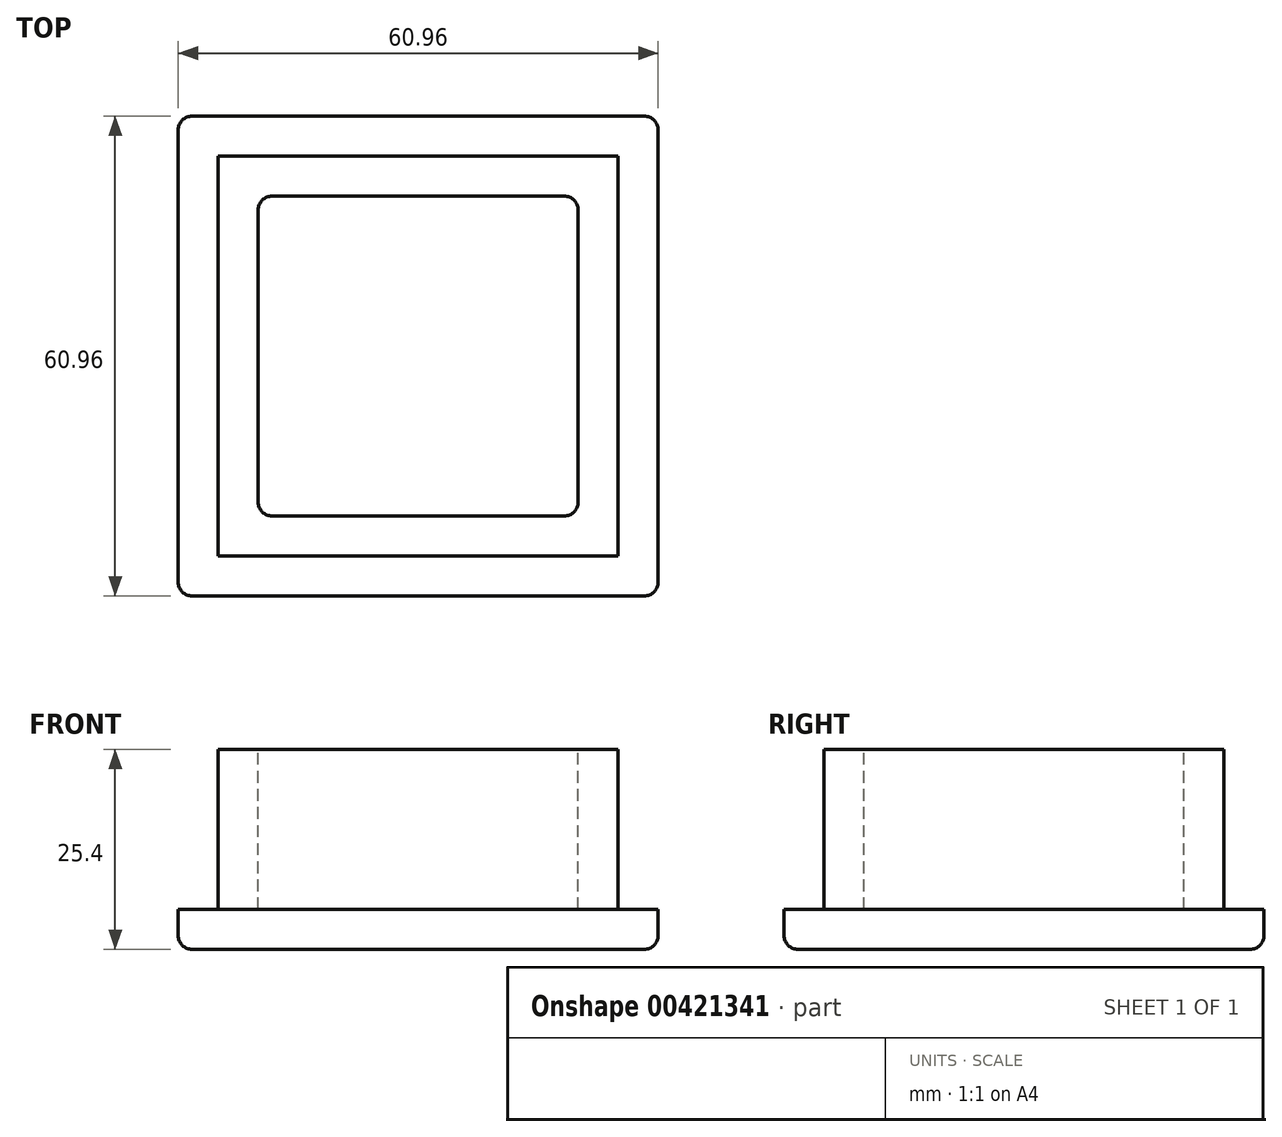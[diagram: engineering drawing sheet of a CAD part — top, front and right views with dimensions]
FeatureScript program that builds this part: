
annotation { "Feature Type Name" : "Feature", "Feature Type Description" : "" }
export const myFeature = defineFeature(function(context is Context, id is Id, definition is map)
    precondition{}
    {
        {
            var Q0;
            Q0=qCreatedBy(makeId("Top.planeOp"),FACE);
            var sketch = newSketch(context, id + "F0", { "sketchPlane" : qUnion([Q0])});
            skLineSegment(sketch, "E0.bottom", {"start": v(0, 0) * mm, "end": v(50.8, 0) * mm});
            skLineSegment(sketch, "E0.top", {"start": v(0, 50.8) * mm, "end": v(50.8, 50.8) * mm});
            skLineSegment(sketch, "E0.left", {"start": v(0, 0) * mm, "end": v(0, 50.8) * mm});
            skLineSegment(sketch, "E0.right", {"start": v(50.8, 0) * mm, "end": v(50.8, 50.8) * mm});
            skSolve(sketch);
        }
        {
            var Q0;
            Q0 = qSketchRegion(id + "F0", true);
            extrude(context, id + "F1", {"entities" : qUnion([Q0]), "depth" : 25.4 * mm});
        }
        {
            var Q0;
            Q0=makeQuery(id+"F1.opExtrude","CAP_FACE",FACE,{"disambiguationData":[OSD([sQuery(id+"F0.wireOp",EDGE,"E0.bottom"),sQuery(id+"F0.wireOp",EDGE,"E0.top"),sQuery(id+"F0.wireOp",EDGE,"E0.left"),sQuery(id+"F0.wireOp",EDGE,"E0.right")])],"isStart":false});
            var sketch = newSketch(context, id + "F2", { "sketchPlane" : qUnion([Q0])});
            skLineSegment(sketch, "E1.bottom", {"start": v(5.08, 5.08) * mm, "end": v(45.72, 5.08) * mm});
            skLineSegment(sketch, "E1.top", {"start": v(5.08, 45.72) * mm, "end": v(45.72, 45.72) * mm});
            skLineSegment(sketch, "E1.left", {"start": v(5.08, 5.08) * mm, "end": v(5.08, 45.72) * mm});
            skLineSegment(sketch, "E1.right", {"start": v(45.72, 5.08) * mm, "end": v(45.72, 45.72) * mm});
            skSolve(sketch);
        }
        {
            var Q0;
            Q0=makeQuery(id+"F2.imprint","IMPRINT",FACE,{"disambiguationData":[TD([[makeQuery(id+"F2.imprint","IMPRINT",EDGE,{"derivedFrom":sQuery(id+"F2.wireOp",EDGE,"E1.bottom")}),1.0]])]});
            extrude(context, id + "F3", {"entities" : qUnion([Q0]), "operationType" : NewBodyOperationType.REMOVE, "oppositeDirection" : true, "depth" : 20.32 * mm});
        }
        {
            var Q0;
            Q0=makeQuery(id+"F3.boolean.opBoolean","COPY",FACE,{"derivedFrom":makeQuery(id+"F3.opExtrude","CAP_FACE",FACE,{"disambiguationData":[OSD([sQuery(id+"F2.wireOp",EDGE,"E1.bottom"),sQuery(id+"F2.wireOp",EDGE,"E1.top"),sQuery(id+"F2.wireOp",EDGE,"E1.left"),sQuery(id+"F2.wireOp",EDGE,"E1.right")])],"isStart":false})});
            var sketch = newSketch(context, id + "F4", { "sketchPlane" : qUnion([Q0])});
            skCircle(sketch, "E2", {"center": v(25.4, 25.4) * mm, "radius": 7.62 * mm});
            skPoint(sketch, "E2.centerSnap0", {"position": v(25.4, 45.72) * mm});
            skSolve(sketch);
        }
        {
            var Q0;
            Q0=makeQuery(id+"F1.opExtrude","CAP_FACE",FACE,{"disambiguationData":[OSD([sQuery(id+"F0.wireOp",EDGE,"E0.bottom"),sQuery(id+"F0.wireOp",EDGE,"E0.top"),sQuery(id+"F0.wireOp",EDGE,"E0.left"),sQuery(id+"F0.wireOp",EDGE,"E0.right")])],"isStart":true});
            var sketch = newSketch(context, id + "F5", { "sketchPlane" : qUnion([Q0])});
            skLineSegment(sketch, "E3.bottom", {"start": v(0, 0) * mm, "end": v(55.88, 0) * mm});
            skLineSegment(sketch, "E3.top", {"start": v(0, -55.88) * mm, "end": v(55.88, -55.88) * mm});
            skLineSegment(sketch, "E3.left", {"start": v(0, 0) * mm, "end": v(0, -55.88) * mm});
            skLineSegment(sketch, "E3.right", {"start": v(55.88, 0) * mm, "end": v(55.88, -55.88) * mm});
            skSolve(sketch);
        }
        {
            var Q0;
            {var subQ4=makeQuery(id+"F1.opExtrude","CAP_EDGE",EDGE,{"disambiguationData":[OSD([sQuery(id+"F0.wireOp",EDGE,"E0.top")])],"isStart":true});Q0=makeQuery(id+"F5.imprint","IMPRINT",FACE,{"disambiguationData":[TD([[makeQuery(id+"F5.imprint","IMPRINT",EDGE,{"derivedFrom":subQ4}),1.0]])]});}
            extrude(context, id + "F6", {"entities" : qUnion([Q0]), "operationType" : NewBodyOperationType.ADD, "depth" : 25.4 * mm});
        }
        {
            var Q0;
            Q0=makeQuery(id+"F6.boolean.opBoolean","MERGE",FACE,{"derivedFrom":[makeQuery(id+"F1.opExtrude","SWEPT_FACE",FACE,{"disambiguationData":[OSD([sQuery(id+"F0.wireOp",EDGE,"E0.left")])]}),makeQuery(id+"F6.opExtrude","SWEPT_FACE",FACE,{"disambiguationData":[OSD([sQuery(id+"F5.wireOp",EDGE,"E3.left")])]})]});
            var sketch = newSketch(context, id + "F7", { "sketchPlane" : qUnion([Q0])});
            skLineSegment(sketch, "E4.bottom", {"start": v(-50.8, -25.4) * mm, "end": v(0, -25.4) * mm});
            skLineSegment(sketch, "E4.top", {"start": v(-50.8, -20.32) * mm, "end": v(0, -20.32) * mm});
            skLineSegment(sketch, "E4.left", {"start": v(-50.8, -25.4) * mm, "end": v(-50.8, -20.32) * mm});
            skLineSegment(sketch, "E4.right", {"start": v(0, -25.4) * mm, "end": v(0, -20.32) * mm});
            skSolve(sketch);
        }
        {
            var Q0;
            Q0=makeQuery(id+"F7.imprint","IMPRINT",FACE,{"disambiguationData":[TD([[makeQuery(id+"F7.imprint","IMPRINT",EDGE,{"derivedFrom":sQuery(id+"F7.wireOp",EDGE,"E4.bottom")}),-1.0]])]});
            extrude(context, id + "F8", {"entities" : qUnion([Q0]), "operationType" : NewBodyOperationType.ADD, "depth" : 5.08 * mm});
        }
        {
            var Q0;
            {var subQ0=sQuery(id+"F0.wireOp",EDGE,"E0.top");Q0=makeQuery(id+"F8.boolean.opBoolean","MERGE",FACE,{"derivedFrom":[makeQuery(id+"F6.boolean.opBoolean","MERGE",FACE,{"derivedFrom":[makeQuery(id+"F1.opExtrude","SWEPT_FACE",FACE,{"disambiguationData":[OSD([subQ0])]}),makeQuery(id+"F6.opExtrude","SWEPT_FACE",FACE,{"disambiguationData":[OSD([subQ0])]})]}),makeQuery(id+"F8.opExtrude","SWEPT_FACE",FACE,{"disambiguationData":[OSD([sQuery(id+"F7.wireOp",EDGE,"E4.left")])]})]});}
            var sketch = newSketch(context, id + "F9", { "sketchPlane" : qUnion([Q0])});
            skLineSegment(sketch, "E5.bottom", {"start": v(5.08, -20.32) * mm, "end": v(-50.8, -20.32) * mm});
            skLineSegment(sketch, "E5.top", {"start": v(5.08, -25.4) * mm, "end": v(-50.8, -25.4) * mm});
            skLineSegment(sketch, "E5.left", {"start": v(5.08, -20.32) * mm, "end": v(5.08, -25.4) * mm});
            skLineSegment(sketch, "E5.right", {"start": v(-50.8, -20.32) * mm, "end": v(-50.8, -25.4) * mm});
            skSolve(sketch);
        }
        {
            var Q0;
            Q0=makeQuery(id+"F9.imprint","IMPRINT",FACE,{"disambiguationData":[TD([[makeQuery(id+"F9.imprint","IMPRINT",EDGE,{"derivedFrom":sQuery(id+"F9.wireOp",EDGE,"E5.top")}),-1.0]])]});
            extrude(context, id + "F10", {"entities" : qUnion([Q0]), "operationType" : NewBodyOperationType.ADD, "depth" : 5.08 * mm});
        }
        {
            var Q0;
            {var subQ0=sQuery(id+"F0.wireOp",EDGE,"E0.right");Q0=makeQuery(id+"F10.boolean.opBoolean","MERGE",FACE,{"derivedFrom":[makeQuery(id+"F6.boolean.opBoolean","MERGE",FACE,{"derivedFrom":[makeQuery(id+"F1.opExtrude","SWEPT_FACE",FACE,{"disambiguationData":[OSD([subQ0])]}),makeQuery(id+"F6.opExtrude","SWEPT_FACE",FACE,{"disambiguationData":[OSD([subQ0])]})]}),makeQuery(id+"F10.opExtrude","SWEPT_FACE",FACE,{"disambiguationData":[OSD([sQuery(id+"F9.wireOp",EDGE,"E5.right")])]})]});}
            var sketch = newSketch(context, id + "F11", { "sketchPlane" : qUnion([Q0])});
            skLineSegment(sketch, "E6.bottom", {"start": v(55.88, -20.32) * mm, "end": v(0, -20.32) * mm});
            skLineSegment(sketch, "E6.top", {"start": v(55.88, -25.4) * mm, "end": v(0, -25.4) * mm});
            skLineSegment(sketch, "E6.left", {"start": v(55.88, -20.32) * mm, "end": v(55.88, -25.4) * mm});
            skLineSegment(sketch, "E6.right", {"start": v(0, -20.32) * mm, "end": v(0, -25.4) * mm});
            skSolve(sketch);
        }
        {
            var Q0;
            Q0=makeQuery(id+"F11.imprint","IMPRINT",FACE,{"disambiguationData":[TD([[makeQuery(id+"F11.imprint","IMPRINT",EDGE,{"derivedFrom":sQuery(id+"F11.wireOp",EDGE,"E6.top")}),1.0]])]});
            extrude(context, id + "F12", {"entities" : qUnion([Q0]), "operationType" : NewBodyOperationType.ADD, "depth" : 5.08 * mm});
        }
        {
            var Q0;
            Q0=makeQuery(id+"F12.boolean.opBoolean","MERGE",FACE,{"derivedFrom":[makeQuery(id+"F8.boolean.opBoolean","MERGE",FACE,{"derivedFrom":[makeQuery(id+"F6.boolean.opBoolean","MERGE",FACE,{"derivedFrom":[makeQuery(id+"F1.opExtrude","SWEPT_FACE",FACE,{"disambiguationData":[OSD([sQuery(id+"F0.wireOp",EDGE,"E0.bottom")])]}),makeQuery(id+"F6.opExtrude","SWEPT_FACE",FACE,{"disambiguationData":[OSD([sQuery(id+"F5.wireOp",EDGE,"E3.bottom")])]})]}),makeQuery(id+"F8.opExtrude","SWEPT_FACE",FACE,{"disambiguationData":[OSD([sQuery(id+"F7.wireOp",EDGE,"E4.right")])]})]}),makeQuery(id+"F12.opExtrude","SWEPT_FACE",FACE,{"disambiguationData":[OSD([sQuery(id+"F11.wireOp",EDGE,"E6.right")])]})]});
            var sketch = newSketch(context, id + "F13", { "sketchPlane" : qUnion([Q0])});
            skLineSegment(sketch, "E7.bottom", {"start": v(55.88, -20.32) * mm, "end": v(-5.08, -20.32) * mm});
            skLineSegment(sketch, "E7.top", {"start": v(55.88, -25.4) * mm, "end": v(-5.08, -25.4) * mm});
            skLineSegment(sketch, "E7.left", {"start": v(55.88, -20.32) * mm, "end": v(55.88, -25.4) * mm});
            skLineSegment(sketch, "E7.right", {"start": v(-5.08, -20.32) * mm, "end": v(-5.08, -25.4) * mm});
            skSolve(sketch);
        }
        {
            var Q0;
            Q0=makeQuery(id+"F13.imprint","IMPRINT",FACE,{"disambiguationData":[TD([[makeQuery(id+"F13.imprint","IMPRINT",EDGE,{"derivedFrom":sQuery(id+"F13.wireOp",EDGE,"E7.top")}),1.0]])]});
            extrude(context, id + "F14", {"entities" : qUnion([Q0]), "operationType" : NewBodyOperationType.ADD, "depth" : 5.08 * mm});
        }
        {
            var Q0;
            Q0=makeQuery(id+"F3.boolean.opBoolean","COPY",FACE,{"derivedFrom":makeQuery(id+"F3.opExtrude","CAP_FACE",FACE,{"disambiguationData":[OSD([sQuery(id+"F2.wireOp",EDGE,"E1.bottom"),sQuery(id+"F2.wireOp",EDGE,"E1.top"),sQuery(id+"F2.wireOp",EDGE,"E1.left"),sQuery(id+"F2.wireOp",EDGE,"E1.right")])],"isStart":false})});
            extrude(context, id + "F15", {"entities" : qUnion([Q0]), "operationType" : NewBodyOperationType.REMOVE, "oppositeDirection" : true, "depth" : 25.4 * mm});
        }
        {
            var Q0;
            Q0=makeQuery(id+"F1.opExtrude","CAP_FACE",FACE,{"disambiguationData":[OSD([sQuery(id+"F0.wireOp",EDGE,"E0.bottom"),sQuery(id+"F0.wireOp",EDGE,"E0.top"),sQuery(id+"F0.wireOp",EDGE,"E0.left"),sQuery(id+"F0.wireOp",EDGE,"E0.right")])],"isStart":false});
            var Q1;
            Q1=makeQuery(id+"FlgKvXzoSUtQgZy_1.opExtrude","CAP_FACE",FACE,{"disambiguationData":[OSD([sQuery(id+"F4.wireOp",EDGE,"E2")])],"isStart":false});
            extrude(context, id + "F16", {"entities" : qUnion([Q0, Q1]), "operationType" : NewBodyOperationType.REMOVE, "oppositeDirection" : true, "depth" : 25.4 * mm});
        }
        {
            var Q0;
            Q0=makeQuery(id+"F14.opExtrude","CAP_EDGE",EDGE,{"disambiguationData":[OSD([sQuery(id+"F13.wireOp",EDGE,"E7.right")])],"isStart":false});
            var Q1;
            Q1=makeQuery(id+"F14.opExtrude","CAP_EDGE",EDGE,{"disambiguationData":[OSD([sQuery(id+"F13.wireOp",EDGE,"E7.left")])],"isStart":false});
            var Q2;
            Q2=makeQuery(id+"F12.opExtrude","CAP_EDGE",EDGE,{"disambiguationData":[OSD([sQuery(id+"F11.wireOp",EDGE,"E6.left")])],"isStart":false});
            var Q3;
            Q3=makeQuery(id+"F10.opExtrude","CAP_EDGE",EDGE,{"disambiguationData":[OSD([sQuery(id+"F9.wireOp",EDGE,"E5.left")])],"isStart":false});
            fillet(context, id + "F17", {"entities" : qUnion([Q0, Q1, Q2, Q3]), "radius" : 1.78 * mm, "tangentPropagation" : true, "allowEdgeOverflow" : false});
        }
        {
            var Q0;
            {var subQ0=sQuery(id+"F2.wireOp",EDGE,"E1.right");var subQ1=sQuery(id+"F2.wireOp",EDGE,"E1.top");Q0=makeQuery(id+"F15.boolean.opBoolean","MERGE",EDGE,{"derivedFrom":[makeQuery(id+"F3.boolean.opBoolean","COPY",EDGE,{"derivedFrom":makeQuery(id+"F3.opExtrude","SWEPT_EDGE",EDGE,{"disambiguationData":[OSD([subQ1,subQ0])]})}),makeQuery(id+"F15.opExtrude","SWEPT_EDGE",EDGE,{"disambiguationData":[OSD([subQ1,subQ0])]})]});}
            var Q1;
            {var subQ0=sQuery(id+"F2.wireOp",EDGE,"E1.left");var subQ1=sQuery(id+"F2.wireOp",EDGE,"E1.top");Q1=makeQuery(id+"F15.boolean.opBoolean","MERGE",EDGE,{"derivedFrom":[makeQuery(id+"F3.boolean.opBoolean","COPY",EDGE,{"derivedFrom":makeQuery(id+"F3.opExtrude","SWEPT_EDGE",EDGE,{"disambiguationData":[OSD([subQ1,subQ0])]})}),makeQuery(id+"F15.opExtrude","SWEPT_EDGE",EDGE,{"disambiguationData":[OSD([subQ1,subQ0])]})]});}
            var Q2;
            {var subQ0=sQuery(id+"F2.wireOp",EDGE,"E1.left");var subQ1=sQuery(id+"F2.wireOp",EDGE,"E1.bottom");Q2=makeQuery(id+"F15.boolean.opBoolean","MERGE",EDGE,{"derivedFrom":[makeQuery(id+"F3.boolean.opBoolean","COPY",EDGE,{"derivedFrom":makeQuery(id+"F3.opExtrude","SWEPT_EDGE",EDGE,{"disambiguationData":[OSD([subQ1,subQ0])]})}),makeQuery(id+"F15.opExtrude","SWEPT_EDGE",EDGE,{"disambiguationData":[OSD([subQ1,subQ0])]})]});}
            var Q3;
            {var subQ0=sQuery(id+"F2.wireOp",EDGE,"E1.right");var subQ1=sQuery(id+"F2.wireOp",EDGE,"E1.bottom");Q3=makeQuery(id+"F15.boolean.opBoolean","MERGE",EDGE,{"derivedFrom":[makeQuery(id+"F3.boolean.opBoolean","COPY",EDGE,{"derivedFrom":makeQuery(id+"F3.opExtrude","SWEPT_EDGE",EDGE,{"disambiguationData":[OSD([subQ1,subQ0])]})}),makeQuery(id+"F15.opExtrude","SWEPT_EDGE",EDGE,{"disambiguationData":[OSD([subQ1,subQ0])]})]});}
            fillet(context, id + "F18", {"entities" : qUnion([Q0, Q1, Q2, Q3]), "radius" : 1.78 * mm, "tangentPropagation" : true, "allowEdgeOverflow" : false});
        }
        {
            var Q0;
            Q0=makeQuery(id+"F14.opExtrude","CAP_EDGE",EDGE,{"disambiguationData":[OSD([sQuery(id+"F13.wireOp",EDGE,"E7.top")])],"isStart":false});
            var Q1;
            Q1=makeQuery(id+"F14.boolean.opBoolean","MERGE",EDGE,{"derivedFrom":[makeQuery(id+"F10.boolean.opBoolean","MERGE",EDGE,{"derivedFrom":[makeQuery(id+"F8.opExtrude","CAP_EDGE",EDGE,{"disambiguationData":[OSD([sQuery(id+"F7.wireOp",EDGE,"E4.bottom")])],"isStart":false}),makeQuery(id+"F10.opExtrude","SWEPT_EDGE",EDGE,{"disambiguationData":[OSD([sQuery(id+"F9.wireOp",EDGE,"E5.top"),sQuery(id+"F9.wireOp",EDGE,"E5.left")])]})]}),makeQuery(id+"F14.opExtrude","SWEPT_EDGE",EDGE,{"disambiguationData":[OSD([sQuery(id+"F13.wireOp",EDGE,"E7.top"),sQuery(id+"F13.wireOp",EDGE,"E7.right")])]})]});
            var Q2;
            Q2=makeQuery(id+"F14.boolean.opBoolean","MERGE",EDGE,{"derivedFrom":[makeQuery(id+"F12.opExtrude","CAP_EDGE",EDGE,{"disambiguationData":[OSD([sQuery(id+"F11.wireOp",EDGE,"E6.top")])],"isStart":false}),makeQuery(id+"F14.opExtrude","SWEPT_EDGE",EDGE,{"disambiguationData":[OSD([sQuery(id+"F13.wireOp",EDGE,"E7.top"),sQuery(id+"F13.wireOp",EDGE,"E7.left")])]})]});
            var Q3;
            Q3=makeQuery(id+"F12.boolean.opBoolean","MERGE",EDGE,{"derivedFrom":[makeQuery(id+"F10.opExtrude","CAP_EDGE",EDGE,{"disambiguationData":[OSD([sQuery(id+"F9.wireOp",EDGE,"E5.top")])],"isStart":false}),makeQuery(id+"F12.opExtrude","SWEPT_EDGE",EDGE,{"disambiguationData":[OSD([sQuery(id+"F11.wireOp",EDGE,"E6.top"),sQuery(id+"F11.wireOp",EDGE,"E6.left")])]})]});
            var Q4;
            Q4=makeQuery(id+"F17.opFillet","BLEND_EDGE",EDGE,{"blendedFrom":[makeQuery(id+"F12.opExtrude","CAP_EDGE",EDGE,{"disambiguationData":[OSD([sQuery(id+"F11.wireOp",EDGE,"E6.left")])],"isStart":false}),makeQuery(id+"F14.boolean.opBoolean","MERGE",FACE,{"derivedFrom":[makeQuery(id+"F12.boolean.opBoolean","MERGE",FACE,{"derivedFrom":[makeQuery(id+"F10.boolean.opBoolean","MERGE",FACE,{"derivedFrom":[makeQuery(id+"F8.boolean.opBoolean","MERGE",FACE,{"derivedFrom":[makeQuery(id+"F6.opExtrude","CAP_FACE",FACE,{"disambiguationData":[OSD([sQuery(id+"F0.wireOp",EDGE,"E0.top"),sQuery(id+"F0.wireOp",EDGE,"E0.right"),sQuery(id+"F5.wireOp",EDGE,"E3.bottom"),sQuery(id+"F5.wireOp",EDGE,"E3.left")])],"isStart":false}),makeQuery(id+"F8.opExtrude","SWEPT_FACE",FACE,{"disambiguationData":[OSD([sQuery(id+"F7.wireOp",EDGE,"E4.bottom")])]})]}),makeQuery(id+"F10.opExtrude","SWEPT_FACE",FACE,{"disambiguationData":[OSD([sQuery(id+"F9.wireOp",EDGE,"E5.top")])]})]}),makeQuery(id+"F12.opExtrude","SWEPT_FACE",FACE,{"disambiguationData":[OSD([sQuery(id+"F11.wireOp",EDGE,"E6.top")])]})]}),makeQuery(id+"F14.opExtrude","SWEPT_FACE",FACE,{"disambiguationData":[OSD([sQuery(id+"F13.wireOp",EDGE,"E7.top")])]})]})],"blendedInto":[makeQuery(id+"F14.boolean.opBoolean","MERGE",FACE,{"derivedFrom":[makeQuery(id+"F12.boolean.opBoolean","MERGE",FACE,{"derivedFrom":[makeQuery(id+"F10.boolean.opBoolean","MERGE",FACE,{"derivedFrom":[makeQuery(id+"F8.boolean.opBoolean","MERGE",FACE,{"derivedFrom":[makeQuery(id+"F6.opExtrude","CAP_FACE",FACE,{"disambiguationData":[OSD([sQuery(id+"F0.wireOp",EDGE,"E0.top"),sQuery(id+"F0.wireOp",EDGE,"E0.right"),sQuery(id+"F5.wireOp",EDGE,"E3.bottom"),sQuery(id+"F5.wireOp",EDGE,"E3.left")])],"isStart":false}),makeQuery(id+"F8.opExtrude","SWEPT_FACE",FACE,{"disambiguationData":[OSD([sQuery(id+"F7.wireOp",EDGE,"E4.bottom")])]})]}),makeQuery(id+"F10.opExtrude","SWEPT_FACE",FACE,{"disambiguationData":[OSD([sQuery(id+"F9.wireOp",EDGE,"E5.top")])]})]}),makeQuery(id+"F12.opExtrude","SWEPT_FACE",FACE,{"disambiguationData":[OSD([sQuery(id+"F11.wireOp",EDGE,"E6.top")])]})]}),makeQuery(id+"F14.opExtrude","SWEPT_FACE",FACE,{"disambiguationData":[OSD([sQuery(id+"F13.wireOp",EDGE,"E7.top")])]})]})]});
            var Q5;
            Q5=makeQuery(id+"F17.opFillet","BLEND_EDGE",EDGE,{"blendedFrom":[makeQuery(id+"F10.opExtrude","CAP_EDGE",EDGE,{"disambiguationData":[OSD([sQuery(id+"F9.wireOp",EDGE,"E5.left")])],"isStart":false}),makeQuery(id+"F14.boolean.opBoolean","MERGE",FACE,{"derivedFrom":[makeQuery(id+"F12.boolean.opBoolean","MERGE",FACE,{"derivedFrom":[makeQuery(id+"F10.boolean.opBoolean","MERGE",FACE,{"derivedFrom":[makeQuery(id+"F8.boolean.opBoolean","MERGE",FACE,{"derivedFrom":[makeQuery(id+"F6.opExtrude","CAP_FACE",FACE,{"disambiguationData":[OSD([sQuery(id+"F0.wireOp",EDGE,"E0.top"),sQuery(id+"F0.wireOp",EDGE,"E0.right"),sQuery(id+"F5.wireOp",EDGE,"E3.bottom"),sQuery(id+"F5.wireOp",EDGE,"E3.left")])],"isStart":false}),makeQuery(id+"F8.opExtrude","SWEPT_FACE",FACE,{"disambiguationData":[OSD([sQuery(id+"F7.wireOp",EDGE,"E4.bottom")])]})]}),makeQuery(id+"F10.opExtrude","SWEPT_FACE",FACE,{"disambiguationData":[OSD([sQuery(id+"F9.wireOp",EDGE,"E5.top")])]})]}),makeQuery(id+"F12.opExtrude","SWEPT_FACE",FACE,{"disambiguationData":[OSD([sQuery(id+"F11.wireOp",EDGE,"E6.top")])]})]}),makeQuery(id+"F14.opExtrude","SWEPT_FACE",FACE,{"disambiguationData":[OSD([sQuery(id+"F13.wireOp",EDGE,"E7.top")])]})]})],"blendedInto":[makeQuery(id+"F14.boolean.opBoolean","MERGE",FACE,{"derivedFrom":[makeQuery(id+"F12.boolean.opBoolean","MERGE",FACE,{"derivedFrom":[makeQuery(id+"F10.boolean.opBoolean","MERGE",FACE,{"derivedFrom":[makeQuery(id+"F8.boolean.opBoolean","MERGE",FACE,{"derivedFrom":[makeQuery(id+"F6.opExtrude","CAP_FACE",FACE,{"disambiguationData":[OSD([sQuery(id+"F0.wireOp",EDGE,"E0.top"),sQuery(id+"F0.wireOp",EDGE,"E0.right"),sQuery(id+"F5.wireOp",EDGE,"E3.bottom"),sQuery(id+"F5.wireOp",EDGE,"E3.left")])],"isStart":false}),makeQuery(id+"F8.opExtrude","SWEPT_FACE",FACE,{"disambiguationData":[OSD([sQuery(id+"F7.wireOp",EDGE,"E4.bottom")])]})]}),makeQuery(id+"F10.opExtrude","SWEPT_FACE",FACE,{"disambiguationData":[OSD([sQuery(id+"F9.wireOp",EDGE,"E5.top")])]})]}),makeQuery(id+"F12.opExtrude","SWEPT_FACE",FACE,{"disambiguationData":[OSD([sQuery(id+"F11.wireOp",EDGE,"E6.top")])]})]}),makeQuery(id+"F14.opExtrude","SWEPT_FACE",FACE,{"disambiguationData":[OSD([sQuery(id+"F13.wireOp",EDGE,"E7.top")])]})]})]});
            var Q6;
            Q6=makeQuery(id+"F17.opFillet","BLEND_EDGE",EDGE,{"blendedFrom":[makeQuery(id+"F14.opExtrude","CAP_EDGE",EDGE,{"disambiguationData":[OSD([sQuery(id+"F13.wireOp",EDGE,"E7.right")])],"isStart":false}),makeQuery(id+"F14.boolean.opBoolean","MERGE",FACE,{"derivedFrom":[makeQuery(id+"F12.boolean.opBoolean","MERGE",FACE,{"derivedFrom":[makeQuery(id+"F10.boolean.opBoolean","MERGE",FACE,{"derivedFrom":[makeQuery(id+"F8.boolean.opBoolean","MERGE",FACE,{"derivedFrom":[makeQuery(id+"F6.opExtrude","CAP_FACE",FACE,{"disambiguationData":[OSD([sQuery(id+"F0.wireOp",EDGE,"E0.top"),sQuery(id+"F0.wireOp",EDGE,"E0.right"),sQuery(id+"F5.wireOp",EDGE,"E3.bottom"),sQuery(id+"F5.wireOp",EDGE,"E3.left")])],"isStart":false}),makeQuery(id+"F8.opExtrude","SWEPT_FACE",FACE,{"disambiguationData":[OSD([sQuery(id+"F7.wireOp",EDGE,"E4.bottom")])]})]}),makeQuery(id+"F10.opExtrude","SWEPT_FACE",FACE,{"disambiguationData":[OSD([sQuery(id+"F9.wireOp",EDGE,"E5.top")])]})]}),makeQuery(id+"F12.opExtrude","SWEPT_FACE",FACE,{"disambiguationData":[OSD([sQuery(id+"F11.wireOp",EDGE,"E6.top")])]})]}),makeQuery(id+"F14.opExtrude","SWEPT_FACE",FACE,{"disambiguationData":[OSD([sQuery(id+"F13.wireOp",EDGE,"E7.top")])]})]})],"blendedInto":[makeQuery(id+"F14.boolean.opBoolean","MERGE",FACE,{"derivedFrom":[makeQuery(id+"F12.boolean.opBoolean","MERGE",FACE,{"derivedFrom":[makeQuery(id+"F10.boolean.opBoolean","MERGE",FACE,{"derivedFrom":[makeQuery(id+"F8.boolean.opBoolean","MERGE",FACE,{"derivedFrom":[makeQuery(id+"F6.opExtrude","CAP_FACE",FACE,{"disambiguationData":[OSD([sQuery(id+"F0.wireOp",EDGE,"E0.top"),sQuery(id+"F0.wireOp",EDGE,"E0.right"),sQuery(id+"F5.wireOp",EDGE,"E3.bottom"),sQuery(id+"F5.wireOp",EDGE,"E3.left")])],"isStart":false}),makeQuery(id+"F8.opExtrude","SWEPT_FACE",FACE,{"disambiguationData":[OSD([sQuery(id+"F7.wireOp",EDGE,"E4.bottom")])]})]}),makeQuery(id+"F10.opExtrude","SWEPT_FACE",FACE,{"disambiguationData":[OSD([sQuery(id+"F9.wireOp",EDGE,"E5.top")])]})]}),makeQuery(id+"F12.opExtrude","SWEPT_FACE",FACE,{"disambiguationData":[OSD([sQuery(id+"F11.wireOp",EDGE,"E6.top")])]})]}),makeQuery(id+"F14.opExtrude","SWEPT_FACE",FACE,{"disambiguationData":[OSD([sQuery(id+"F13.wireOp",EDGE,"E7.top")])]})]})]});
            var Q7;
            Q7=makeQuery(id+"F17.opFillet","BLEND_EDGE",EDGE,{"blendedFrom":[makeQuery(id+"F14.opExtrude","CAP_EDGE",EDGE,{"disambiguationData":[OSD([sQuery(id+"F13.wireOp",EDGE,"E7.left")])],"isStart":false}),makeQuery(id+"F14.boolean.opBoolean","MERGE",FACE,{"derivedFrom":[makeQuery(id+"F12.boolean.opBoolean","MERGE",FACE,{"derivedFrom":[makeQuery(id+"F10.boolean.opBoolean","MERGE",FACE,{"derivedFrom":[makeQuery(id+"F8.boolean.opBoolean","MERGE",FACE,{"derivedFrom":[makeQuery(id+"F6.opExtrude","CAP_FACE",FACE,{"disambiguationData":[OSD([sQuery(id+"F0.wireOp",EDGE,"E0.top"),sQuery(id+"F0.wireOp",EDGE,"E0.right"),sQuery(id+"F5.wireOp",EDGE,"E3.bottom"),sQuery(id+"F5.wireOp",EDGE,"E3.left")])],"isStart":false}),makeQuery(id+"F8.opExtrude","SWEPT_FACE",FACE,{"disambiguationData":[OSD([sQuery(id+"F7.wireOp",EDGE,"E4.bottom")])]})]}),makeQuery(id+"F10.opExtrude","SWEPT_FACE",FACE,{"disambiguationData":[OSD([sQuery(id+"F9.wireOp",EDGE,"E5.top")])]})]}),makeQuery(id+"F12.opExtrude","SWEPT_FACE",FACE,{"disambiguationData":[OSD([sQuery(id+"F11.wireOp",EDGE,"E6.top")])]})]}),makeQuery(id+"F14.opExtrude","SWEPT_FACE",FACE,{"disambiguationData":[OSD([sQuery(id+"F13.wireOp",EDGE,"E7.top")])]})]})],"blendedInto":[makeQuery(id+"F14.boolean.opBoolean","MERGE",FACE,{"derivedFrom":[makeQuery(id+"F12.boolean.opBoolean","MERGE",FACE,{"derivedFrom":[makeQuery(id+"F10.boolean.opBoolean","MERGE",FACE,{"derivedFrom":[makeQuery(id+"F8.boolean.opBoolean","MERGE",FACE,{"derivedFrom":[makeQuery(id+"F6.opExtrude","CAP_FACE",FACE,{"disambiguationData":[OSD([sQuery(id+"F0.wireOp",EDGE,"E0.top"),sQuery(id+"F0.wireOp",EDGE,"E0.right"),sQuery(id+"F5.wireOp",EDGE,"E3.bottom"),sQuery(id+"F5.wireOp",EDGE,"E3.left")])],"isStart":false}),makeQuery(id+"F8.opExtrude","SWEPT_FACE",FACE,{"disambiguationData":[OSD([sQuery(id+"F7.wireOp",EDGE,"E4.bottom")])]})]}),makeQuery(id+"F10.opExtrude","SWEPT_FACE",FACE,{"disambiguationData":[OSD([sQuery(id+"F9.wireOp",EDGE,"E5.top")])]})]}),makeQuery(id+"F12.opExtrude","SWEPT_FACE",FACE,{"disambiguationData":[OSD([sQuery(id+"F11.wireOp",EDGE,"E6.top")])]})]}),makeQuery(id+"F14.opExtrude","SWEPT_FACE",FACE,{"disambiguationData":[OSD([sQuery(id+"F13.wireOp",EDGE,"E7.top")])]})]})]});
            fillet(context, id + "F19", {"entities" : qUnion([Q0, Q1, Q2, Q3, Q4, Q5, Q6, Q7]), "radius" : 1.78 * mm, "tangentPropagation" : true, "allowEdgeOverflow" : false});
        }
    });
